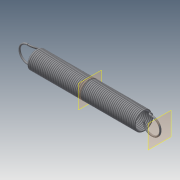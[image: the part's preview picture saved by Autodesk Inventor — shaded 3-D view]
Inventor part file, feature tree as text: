
AUTODESK INVENTOR PART (.ipt)
format: ipt  version: 2020.4 (Build 244396000, 396)  size: 2,441,216 bytes
history: native  units: in
note: dims shown in document units (in); Inventor stores cm internally (conversion verified against a paired STEP export)
features: plane x2, sketch x2, projected_geometry x2, extrude x1, mirror x1, sweep x1
ambient origin geometry x8: Origin, YZ Plane, XZ Plane, XY Plane, X Axis, Y Axis, Z Axis, Center Point
bodies: Solid1 (feature_tree)
feature tree (9):
  extrude  "Extrusion1"  Depth=1.0in TaperAngle=0.0deg
  plane  "Work Plane1"
  mirror  "Mirror1"
  sketch  "Sketch2"  dims[d3=0.1551in d4=0.155in d5=1.07in]
  plane  "Work Plane2"
  sketch  "Sketch1"  dims[d0=1.0935in d1=1.0in d2=0.0in]
  projected_geometry  "Projected Loop1"
  projected_geometry  "Projected Loop2"
  sweep  "Sweep1"
